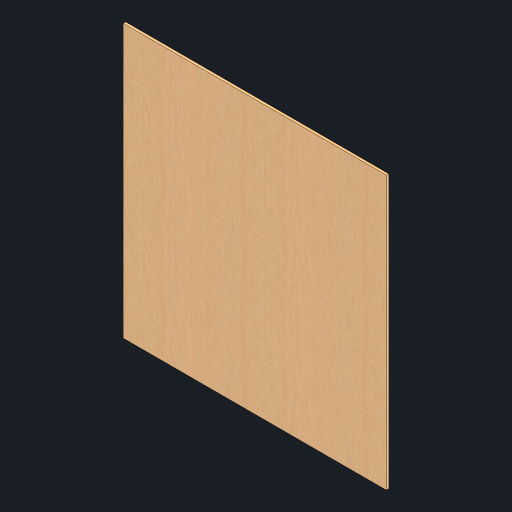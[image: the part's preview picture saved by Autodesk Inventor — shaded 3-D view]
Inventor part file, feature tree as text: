
AUTODESK INVENTOR PART (.ipt)
format: ipt  version: 2024.1 (Build 281209000, 209)  size: 320,512 bytes
history: native  units: mm
features: other x2, extrude x1, sketch x1
ambient origin geometry x8: Origin, YZ Plane, XZ Plane, XY Plane, X Axis, Y Axis, Z Axis, Center Point
bodies: Body1 (feature_tree)
feature tree (4):
  other  "솔리드1"
  extrude  "돌출1"  Depth=550.0mm
  sketch  "스케치1"
  other  "Finish1"
